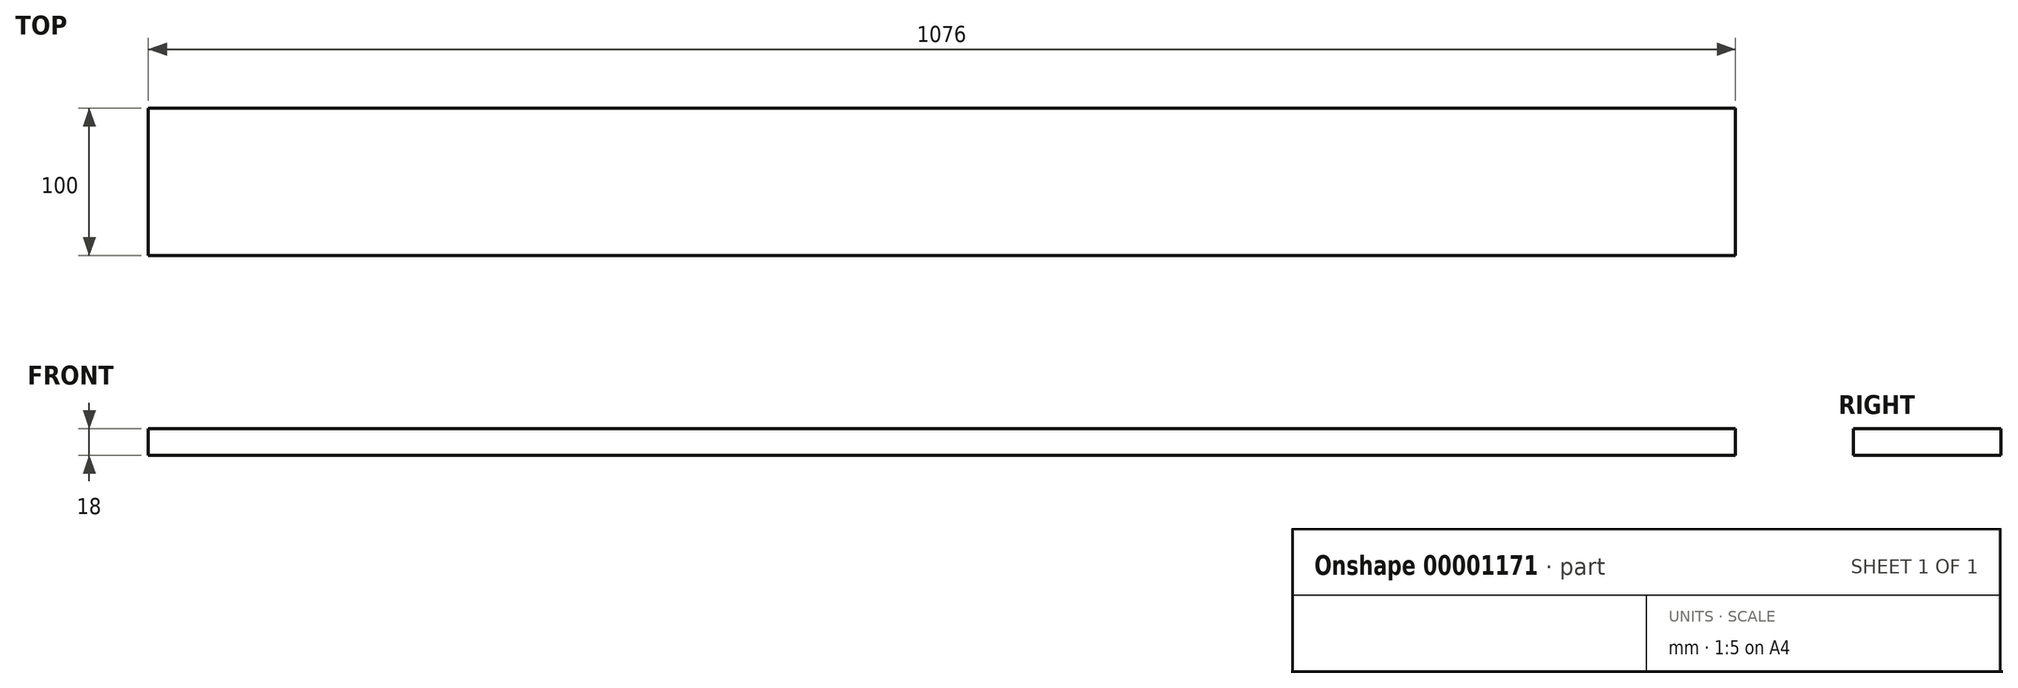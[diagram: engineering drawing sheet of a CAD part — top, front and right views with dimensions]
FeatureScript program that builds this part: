
annotation { "Feature Type Name" : "Feature", "Feature Type Description" : "" }
export const myFeature = defineFeature(function(context is Context, id is Id, definition is map)
    precondition{}
    {
        {
            var Q0;
            Q0=qCreatedBy(makeId("Top.planeOp"),FACE);
            var sketch = newSketch(context, id + "F0", { "sketchPlane" : qUnion([Q0])});
            skLineSegment(sketch, "E0.bottom", {"start": v(0, 0) * mm, "end": v(1076, 0) * mm});
            skLineSegment(sketch, "E0.top", {"start": v(0, 100) * mm, "end": v(1076, 100) * mm});
            skLineSegment(sketch, "E0.left", {"start": v(0, 0) * mm, "end": v(0, 100) * mm});
            skLineSegment(sketch, "E0.right", {"start": v(1076, 0) * mm, "end": v(1076, 100) * mm});
            skSolve(sketch);
        }
        {
            var Q0;
            Q0=qSketchRegion(id+"F0",true);
            extrude(context, id + "F1", {"entities" : qUnion([Q0]), "depth" : 18 * mm});
        }
    });
